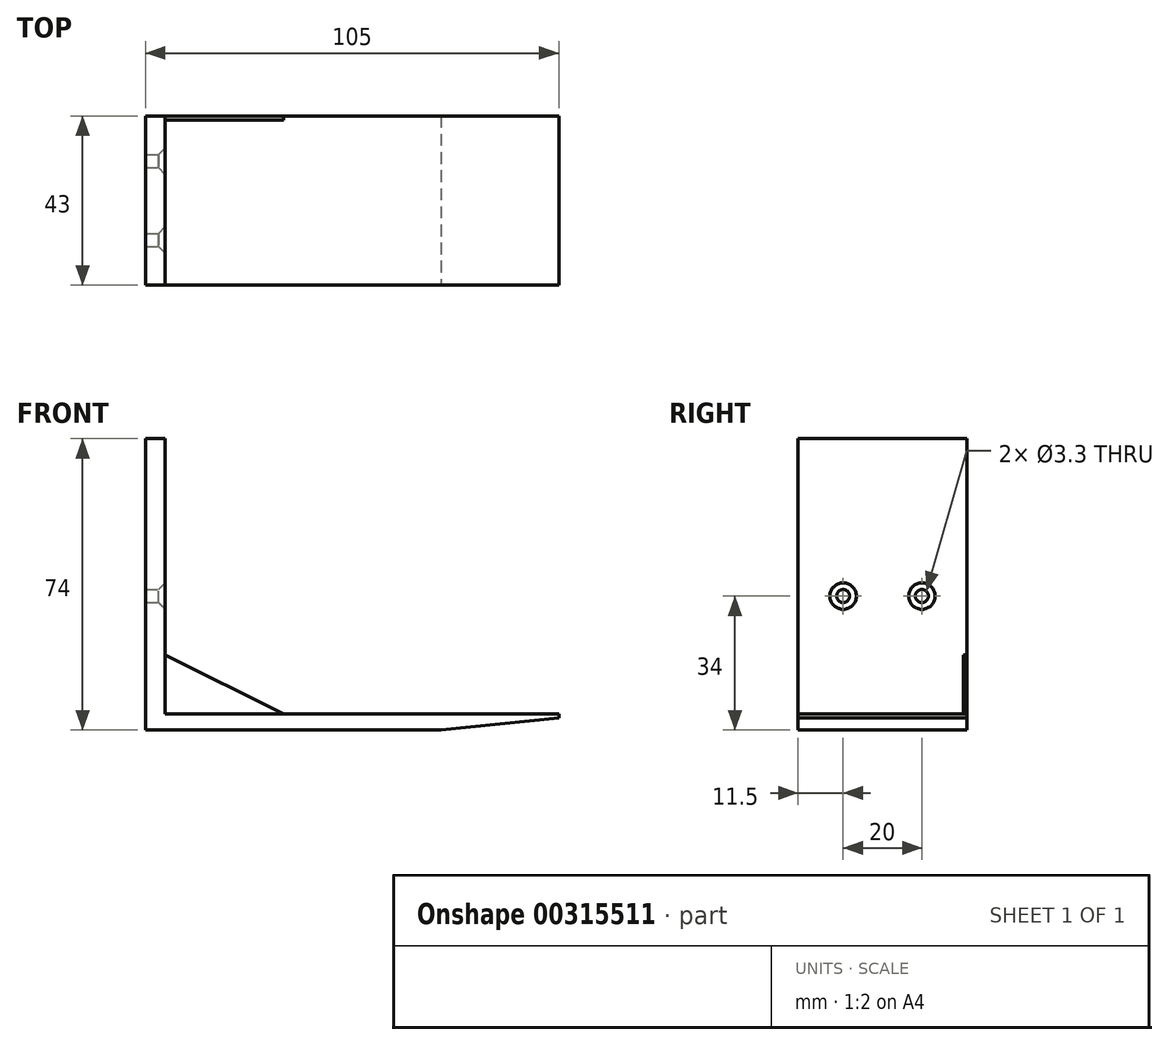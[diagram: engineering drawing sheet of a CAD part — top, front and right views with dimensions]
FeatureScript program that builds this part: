
annotation { "Feature Type Name" : "Feature", "Feature Type Description" : "" }
export const myFeature = defineFeature(function(context is Context, id is Id, definition is map)
    precondition{}
    {
        {
            var Q0;
            Q0=qCreatedBy(makeId("Front.planeOp"),FACE);
            var sketch = newSketch(context, id + "F0", { "sketchPlane" : qUnion([Q0])});
            skLineSegment(sketch, "E0", {"start": v(0, 0) * mm, "end": v(105, 0) * mm});
            skLineSegment(sketch, "E1", {"start": v(105, 0) * mm, "end": v(105, 4) * mm});
            skLineSegment(sketch, "E2", {"start": v(105, 4) * mm, "end": v(5, 4) * mm});
            skLineSegment(sketch, "E3", {"start": v(5, 4) * mm, "end": v(5, 74) * mm});
            skLineSegment(sketch, "E4", {"start": v(5, 74) * mm, "end": v(0, 74) * mm});
            skLineSegment(sketch, "E5", {"start": v(0, 74) * mm, "end": v(0, 0) * mm});
            skSolve(sketch);
        }
        {
            var Q0;
            Q0=makeQuery(id+"F0.imprint","IMPRINT",FACE,{"disambiguationData":[TD([[makeQuery(id+"F0.imprint","IMPRINT",EDGE,{"derivedFrom":sQuery(id+"F0.wireOp",EDGE,"E0")}),1.0]])]});
            extrude(context, id + "F1", {"entities" : qUnion([Q0]), "oppositeDirection" : true, "depth" : 43 * mm});
        }
        {
            var Q0;
            Q0=makeQuery(id+"F1.opExtrude","SWEPT_FACE",FACE,{"disambiguationData":[OSD([sQuery(id+"F0.wireOp",EDGE,"E3")])]});
            var sketch = newSketch(context, id + "F2", { "sketchPlane" : qUnion([Q0])});
            skLineSegment(sketch, "E6.0", {"start": v(43, 74) * mm, "end": v(0, 74) * mm});
            skLineSegment(sketch, "E7", {"start": v(21.5, 74) * mm, "end": v(21.5, 34) * mm});
            skPoint(sketch, "E7.endSnap0", {"position": v(21.5, 74) * mm});
            skLineSegment(sketch, "E8", {"start": v(21.5, 34) * mm, "end": v(31.5, 34) * mm});
            skLineSegment(sketch, "E9.MirrorCS", {"start": v(21.5, 34) * mm, "end": v(11.5, 34) * mm});
            skSolve(sketch);
        }
        {
            var Q0;
            Q0=sQuery(id+"F2.wireOp",VERTEX,"E8.end");
            var Q1;
            Q1=sQuery(id+"F2.wireOp",VERTEX,"E9.MirrorCS.end");
            var Q2;
            Q2=makeQuery(id+"F1.opExtrude","SWEPT_BODY",BODY,{"disambiguationData":[OSD([sQuery(id+"F0.wireOp",EDGE,"E0"),sQuery(id+"F0.wireOp",EDGE,"E1"),sQuery(id+"F0.wireOp",EDGE,"E2"),sQuery(id+"F0.wireOp",EDGE,"E3"),sQuery(id+"F0.wireOp",EDGE,"E4"),sQuery(id+"F0.wireOp",EDGE,"E5")])]});
            hole(context, id + "F3", {"style" : HoleStyle.C_SINK, "endStyle" : HoleEndStyle.THROUGH, "standardTappedOrClearance" : lookupTablePath({ "standard" : "ISO", "fit" : "Normal", "size" : "M3", "type" : "Clearance" }), "standardBlindInLast" : lookupTablePath({ "fit" : "Standard", "standard" : "ISO", "size" : "M3", "type" : "Clearance" }), "holeDiameter" : 3.3 * mm, "cSinkDiameter" : 6.72 * mm, "cSinkAngle" : 90 * degree, "tappedDepth" : 12 * mm, "tapClearance" : 3, "locations" : qUnion([Q0, Q1]), "scope" : qUnion([Q2])});
        }
        {
            var Q0;
            Q0=makeQuery(id+"F1.opExtrude","SWEPT_EDGE",EDGE,{"disambiguationData":[OSD([sQuery(id+"F0.wireOp",EDGE,"E0"),sQuery(id+"F0.wireOp",EDGE,"E1")])]});
            chamfer(context, id + "F4", {"entities" : qUnion([Q0]), "chamferType" : ChamferType.TWO_OFFSETS, "width1" : 30 * mm, "oppositeDirection" : false, "width2" : 3 * mm, "tangentPropagation" : true});
        }
        {
            var Q0;
            Q0=makeQuery(id+"F1.opExtrude","CAP_FACE",FACE,{"disambiguationData":[OSD([sQuery(id+"F0.wireOp",EDGE,"E0"),sQuery(id+"F0.wireOp",EDGE,"E1"),sQuery(id+"F0.wireOp",EDGE,"E2"),sQuery(id+"F0.wireOp",EDGE,"E3"),sQuery(id+"F0.wireOp",EDGE,"E4"),sQuery(id+"F0.wireOp",EDGE,"E5")])],"isStart":false});
            var sketch = newSketch(context, id + "F5", { "sketchPlane" : qUnion([Q0])});
            skLineSegment(sketch, "E10.0", {"start": v(-5, 4) * mm, "end": v(-5, 74) * mm});
            skLineSegment(sketch, "E11.0", {"start": v(-105, 4) * mm, "end": v(-5, 4) * mm});
            skLineSegment(sketch, "E12", {"start": v(-5, 19) * mm, "end": v(-35, 4) * mm});
            skSolve(sketch);
        }
        {
            var Q0;
            {var subQ3=sQuery(id+"F5.wireOp",EDGE,"E12");Q0=makeQuery(id+"F5.imprint","IMPRINT",FACE,{"disambiguationData":[TD([[makeQuery(id+"F5.imprint","IMPRINT",EDGE,{"derivedFrom":subQ3}),1.0]])]});}
            extrude(context, id + "F6", {"entities" : qUnion([Q0]), "operationType" : NewBodyOperationType.ADD, "oppositeDirection" : true, "depth" : 1 * mm});
        }
    });
